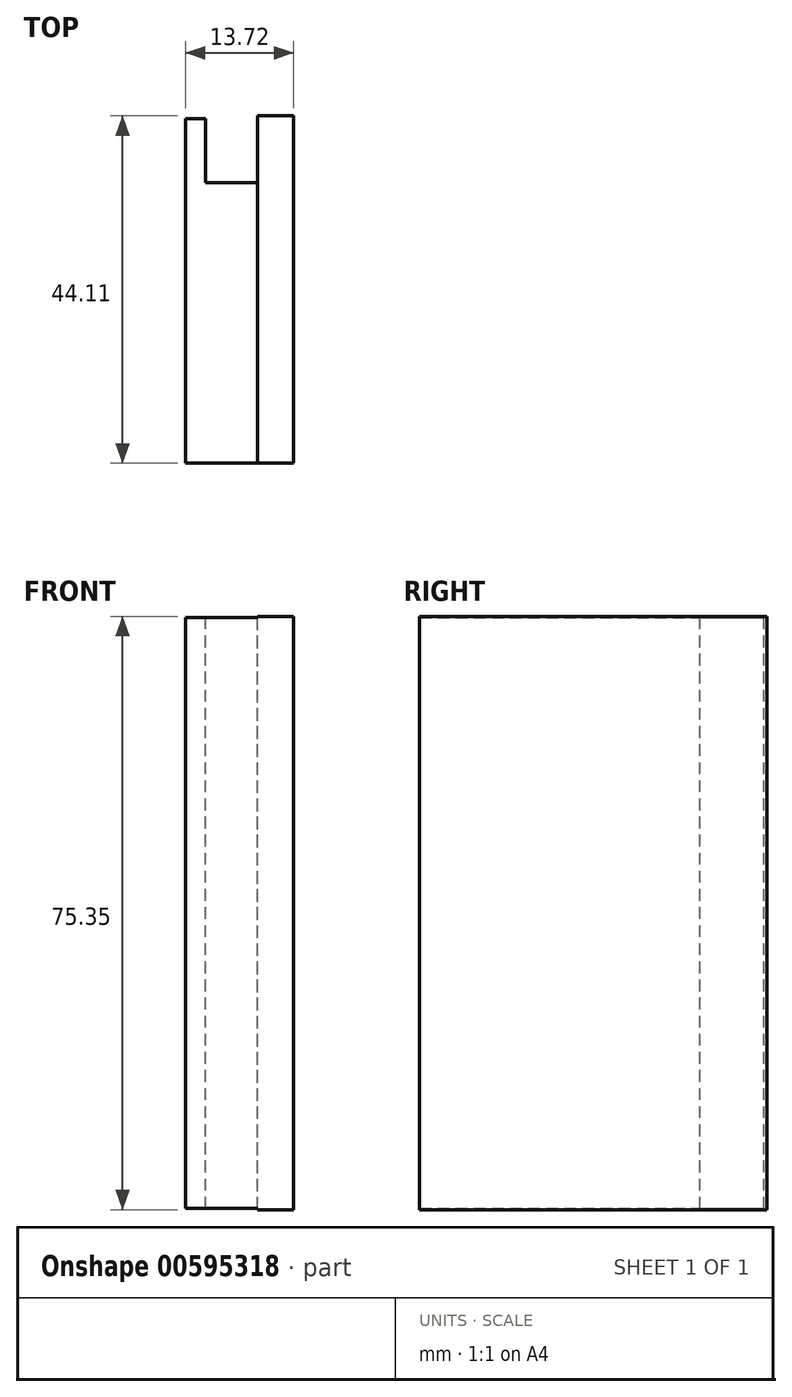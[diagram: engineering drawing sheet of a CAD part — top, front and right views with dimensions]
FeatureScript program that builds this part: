
annotation { "Feature Type Name" : "Feature", "Feature Type Description" : "" }
export const myFeature = defineFeature(function(context is Context, id is Id, definition is map)
    precondition{}
    {
        {
            var Q0;
            Q0=qCreatedBy(makeId("Right.planeOp"),FACE);
            var sketch = newSketch(context, id + "F0", { "sketchPlane" : qUnion([Q0])});
            skLineSegment(sketch, "E0.bottom", {"start": v(-24, -22.73) * mm, "end": v(19.74, -22.73) * mm});
            skLineSegment(sketch, "E0.top", {"start": v(-24, 52.34) * mm, "end": v(19.74, 52.34) * mm});
            skLineSegment(sketch, "E0.left", {"start": v(-24, -22.73) * mm, "end": v(-24, 52.34) * mm});
            skLineSegment(sketch, "E0.right", {"start": v(19.74, -22.73) * mm, "end": v(19.74, 52.34) * mm});
            skSolve(sketch);
        }
        {
            var Q0;
            Q0 = qSketchRegion(id + "F0", true);
            extrude(context, id + "F1", {"entities" : qUnion([Q0]), "depth" : 2.54 * mm, "offsetDistance" : 25.4 * mm});
        }
        {
            var Q0;
            Q0=makeQuery(id+"F1.opExtrude","CAP_FACE",FACE,{"disambiguationData":[OSD([sQuery(id+"F0.wireOp",EDGE,"E0.bottom"),sQuery(id+"F0.wireOp",EDGE,"E0.top"),sQuery(id+"F0.wireOp",EDGE,"E0.left"),sQuery(id+"F0.wireOp",EDGE,"E0.right")])],"isStart":false});
            var sketch = newSketch(context, id + "F2", { "sketchPlane" : qUnion([Q0])});
            skLineSegment(sketch, "E1.bottom", {"start": v(-24, -22.73) * mm, "end": v(11.63, -22.73) * mm});
            skLineSegment(sketch, "E1.top", {"start": v(-24, 52.34) * mm, "end": v(11.63, 52.34) * mm});
            skLineSegment(sketch, "E1.left", {"start": v(-24, -22.73) * mm, "end": v(-24, 52.34) * mm});
            skLineSegment(sketch, "E1.right", {"start": v(11.63, -22.73) * mm, "end": v(11.63, 52.34) * mm});
            skSolve(sketch);
        }
        {
            var Q0;
            Q0 = qSketchRegion(id + "F2", true);
            extrude(context, id + "F3", {"entities" : qUnion([Q0]), "operationType" : NewBodyOperationType.ADD, "depth" : 6.6 * mm, "offsetDistance" : 25.4 * mm});
        }
        {
            var Q0;
            Q0=makeQuery(id+"F3.opExtrude","CAP_FACE",FACE,{"disambiguationData":[OSD([sQuery(id+"F2.wireOp",EDGE,"E1.bottom"),sQuery(id+"F2.wireOp",EDGE,"E1.top"),sQuery(id+"F2.wireOp",EDGE,"E1.left"),sQuery(id+"F2.wireOp",EDGE,"E1.right")])],"isStart":false});
            var sketch = newSketch(context, id + "F4", { "sketchPlane" : qUnion([Q0])});
            skLineSegment(sketch, "E2.bottom", {"start": v(-24, -22.87) * mm, "end": v(20.1, -22.87) * mm});
            skLineSegment(sketch, "E2.top", {"start": v(-24, 52.48) * mm, "end": v(20.1, 52.48) * mm});
            skLineSegment(sketch, "E2.left", {"start": v(-24, -22.87) * mm, "end": v(-24, 52.48) * mm});
            skLineSegment(sketch, "E2.right", {"start": v(20.1, -22.87) * mm, "end": v(20.1, 52.48) * mm});
            skSolve(sketch);
        }
        {
            var Q0;
            Q0 = qSketchRegion(id + "F4", true);
            extrude(context, id + "F5", {"entities" : qUnion([Q0]), "operationType" : NewBodyOperationType.ADD, "depth" : 4.57 * mm, "offsetDistance" : 25.4 * mm});
        }
        {
            var Q0;
            Q0=makeQuery(id+"F5.opExtrude","CAP_FACE",FACE,{"disambiguationData":[OSD([sQuery(id+"F4.wireOp",EDGE,"E2.bottom"),sQuery(id+"F4.wireOp",EDGE,"E2.top"),sQuery(id+"F4.wireOp",EDGE,"E2.left"),sQuery(id+"F4.wireOp",EDGE,"E2.right")])],"isStart":false});
            var sketch = newSketch(context, id + "F6", { "sketchPlane" : qUnion([Q0])});
            skText(sketch, "E3", { "text": "BOOK", "fontName": "OpenSans-Regular.ttf"});
            const initialGuessF6  = {"E3": [-0.02492, 0.03554, 1, 0, 0.0116]};
            skSetInitialGuess(sketch, initialGuessF6);
            skSolve(sketch);
        }
        {
            var Q0;
            Q0 = qConstructionFilter(qBodyType(qCreatedBy(id + "F6" ,EDGE), BodyType.WIRE), ConstructionObject.NO);
            extrude(context, id + "F7", {"bodyType" : ToolBodyType.SURFACE, "surfaceEntities" : qUnion([Q0]), "depth" : 1.52 * mm, "offsetDistance" : 25.4 * mm});
        }
    });
